# Revit family: CH-EU-OU
name_source: partatom
category: Lighting Fixtures
revit_build: Autodesk Revit Architecture 2012 (Build: 20110309_2315(x64)
units: mm (PartAtom-declared; Revit-internal decimal feet)

## types (41) — shared parameters
Ballast = White
Color Filter = 16777215
Default Elevation = 48"
Description = Low to medium mounting heights.
Dimming Lamp Color Temperature Shift = <None>
Emit from Line Length = 10"
Lamp = 1
Manufacturer = Devine Lighting
Manufacturer Fax = 864-678-1065
Model = CH EU/CH OU
Product Documentation Link = http://www.hubbellindustrial.com
Product Page URL = http://www.hubbellindustrial.com
Reflector = Aluminium
Tilt Angle = 0.00°
URL = http://www.hubbellindustrial.com
Wattage Comments = 250W/ 320W/ 350W/ 400W/ 450W/ 750W

## per-type parameters (varying)
| type | Photometric Web File |
| CH25Hxx-EU LU/LP: 1@20500 SC @2/@4: 1.3/1.4 | HP06475.IES |
| CH25Hxx-EU LU/LP: 1@20500 SC @2/@4: 1.5/1.5 | HP06470.IES |
| CH25Hxx-EU LU/LP: 1@20500 SC @2/@4: 1.9/1.6 | HP06467.IES |
| CH25Hxx-EU LU/LP: 1@20500 SC @2/@4: 2.1/1.7 | HP06474.IES |
| CH25Hxx-EU LU/LP: 1@20500 SC @2/@4: 2.2/1.8 | HP06471.IES |
| CH25Hxx-OU/ENC LU/LP: 1@20500 SC @2/@4: 1.4/1.4 | HP06479.IES |
| CH25Hxx-OU/ENC LU/LP: 1@20500 SC @2/@4: 1.6/1.5 | HP06477.IES |
| CH25Hxx-OU/ENC LU/LP: 1@20500 SC @2/@4: 2.0/1.7 | HP06476.IES |
| CH25Hxx-OU/ENC LU/LP: 1@20500 SC @2/@4: 2.2/1.8 | HP06478.IES |
| CH40Hxx-EU LU/LP: 1@36000 SC @2/@4: 1.1/1.2 | HP06190.IES |
| CH40Hxx-EU LU/LP: 1@36000 SC @2/@4: 1.2/1.4 | HP06381.IES |
| CH40Hxx-EU LU/LP: 1@36000 SC @2/@4: 1.5/1.5 | HP06188.IES |
| CH40Hxx-EU LU/LP: 1@36000 SC @2/@4: 1.8/1.6 | HP06189.IES |
| CH40Hxx-EU LU/LP: 1@36000 SC @2/@4: 2.0/1.7 | HP06382.IES |
| CH40Hxx-EU LU/LP: 1@34200 SC @2/@4: 1.7/1.5 | HP07312.IES |
| CH40Hxx-EU LU/LP: 1@34200 SC @2/@4: 1.9/1.7 | HP07311.IES |
| CH40Hxx-OU LU/LP: 1@34200 SC @2/@4: 1.4/1.4 | HP07310.IES |
| CH40Hxx-OU LU/LP: 1@34200 SC @2/@4: 1.7/1.6 | HP07309.IES |
| CH40Hxx-OU LU/LP: 1@34200 SC @2/@4: 2.0/1.7 | HP07308.IES |
| CH40Hxx-OU LU/LP: 1@36000 SC @2/@4: 1.2/1.3 | HP06383.IES |
| CH40Hxx-OU LU/LP: 1@36000 SC @2/@4: 1.4/1.5 | HP06164.IES |
| CH40Hxx-OU LU/LP: 1@36000 SC @2/@4: 1.7/1.6 | HP06163.IES |
| CH40Hxx-OU LU/LP: 1@36000 SC @2/@4: 2.1/1.7 | HP06384.IES |
| CH40Hxx-OU LU/LP: 1@36000 SC @2/@4: 2.2/1.8 | HP06385.IES |
| CH40Sxx-EU LU/LP: 1@50000 SC @2/@4: 0.7/1.1 | HP06379.IES |
| CH40Sxx-EU LU/LP: 1@50000 SC @2/@4: 1.0/1.3 | HP06193.IES |
| CH40Sxx-EU LU/LP: 1@50000 SC @2/@4: 1.3/1.5 | HP06191.IES |
| CH40Sxx-EU LU/LP: 1@50000 SC @2/@4: 1.7/1.6 | HP06192.IES |
| CH40Sxx-EU LU/LP: 1@50000 SC @2/@4: 2.0/1.8 | HP06380.IES |
| CH40Sxx-OU LU/LP: 1@50000 SC @2/@4: 0.8/1.2 | HP06374.IES |
| CH40Sxx-OU LU/LP: 1@50000 SC @2/@4: 1.2/1.4 | HP06167.IES |
| CH40Sxx-OU LU/LP: 1@50000 SC @2/@4: 1.6/1.6 | HP06166.IES |
| CH40Sxx-OU LU/LP: 1@50000 SC @2/@4: 1.8/1.7 | HP06165.IES |
| CH40Sxx-OU LU/LP: 1@50000 SC @2/@4: 2.1/1.9 | HP06377.IES |
| CH4xHxx-EU-QSS LU/LP: 1@5000 SC @2/@4: 3.7/2.7/2 | HP06996.IES |
| CH4xHxx-OU-QSS LU/LP: 1@5000 SC @2/@4: 3.8/2.7/2 | HP06991.IES |
| CH75Wxx-EU LU/LP: 1@82000 SC @2/@4: 1.0/1.1 | HP09272.IES |
| CH75Wxx-EU LU/LP: 1@82000 SC @2/@4: 1.2/1.2 | HP09279.IES |
| CH75Wxx-EU LU/LP: 1@82000 SC @2/@4: 1.3/1.4 | HP09271.IES |
| CH75Wxx-EU LU/LP: 1@82000 SC @2/@4: 1.5/1.5 | HP09280.IES |
| CH75Wxx-EU LU/LP: 1@82000 SC @2/@4: 1.7/1.6 | HP09281.IES |

## geometry (parser evidence)
native form markers: Blend x1, Sweep x1
no freeform markers — native parametric forms only
